FCSTD DOCUMENT  (FreeCAD 0.17R11580 (Git))
Label: connector_positions
License: All rights reserved
LicenseURL: http://en.wikipedia.org/wiki/All_rights_reserved
objects: Sketcher::SketchObject×2
note: 2 computed .brp shape members not serialized (recipe doc carries the construction recipe); baked Part::Feature solids carry a one-line shape summary decoded from their .brp

FEATURE [Sketcher::SketchObject] Sketch  label="old"
  sketch-geometry (28):
    g0: LineSegment StartX=-20 StartY=20 StartZ=0 EndX=20 EndY=20 EndZ=0
    g1: LineSegment StartX=20 StartY=20 StartZ=0 EndX=20 EndY=-20 EndZ=0
    g2: LineSegment StartX=20 StartY=-20 StartZ=0 EndX=-20 EndY=-20 EndZ=0
    g3: LineSegment StartX=-20 StartY=-20 StartZ=0 EndX=-20 EndY=20 EndZ=0
    g4: Circle CenterX=-9.81 CenterY=-18 CenterZ=0 NormalX=0 NormalY=0 NormalZ=1 Radius=0.5
    g5: Circle CenterX=-7.27 CenterY=-18 CenterZ=0 NormalX=0 NormalY=0 NormalZ=1 Radius=0.5
    g6: LineSegment [constr] StartX=-9.81 StartY=-18 StartZ=0 EndX=-7.27 EndY=-18 EndZ=0
    g7: Circle CenterX=-4.73 CenterY=-18 CenterZ=0 NormalX=0 NormalY=0 NormalZ=1 Radius=0.5
    g8: LineSegment [constr] StartX=-7.27 StartY=-18 StartZ=0 EndX=-4.73 EndY=-18 EndZ=0
    g9: Circle CenterX=-2.19 CenterY=-18 CenterZ=0 NormalX=0 NormalY=0 NormalZ=1 Radius=0.5
    g10: LineSegment [constr] StartX=-4.73 StartY=-18 StartZ=0 EndX=-2.19 EndY=-18 EndZ=0
    g11: Circle CenterX=2.19 CenterY=-18 CenterZ=0 NormalX=0 NormalY=0 NormalZ=1 Radius=0.5
    g12: Circle CenterX=4.73 CenterY=-18 CenterZ=0 NormalX=0 NormalY=0 NormalZ=1 Radius=0.5
    g13: LineSegment [constr] StartX=2.19 StartY=-18 StartZ=0 EndX=4.73 EndY=-18 EndZ=0
    g14: Circle CenterX=7.27 CenterY=-18 CenterZ=0 NormalX=0 NormalY=0 NormalZ=1 Radius=0.5
    g15: LineSegment [constr] StartX=4.73 StartY=-18 StartZ=0 EndX=7.27 EndY=-18 EndZ=0
    g16: Circle CenterX=9.81 CenterY=-18 CenterZ=0 NormalX=0 NormalY=0 NormalZ=1 Radius=0.5
    g17: LineSegment [constr] StartX=7.27 StartY=-18 StartZ=0 EndX=9.81 EndY=-18 EndZ=0
    g18: Circle CenterX=-17.27 CenterY=-18 CenterZ=0 NormalX=0 NormalY=0 NormalZ=1 Radius=0.5
    g19: Circle CenterX=-14.73 CenterY=-18 CenterZ=0 NormalX=0 NormalY=0 NormalZ=1 Radius=0.5
    g20: LineSegment [constr] StartX=-17.27 StartY=-18 StartZ=0 EndX=-14.73 EndY=-18 EndZ=0
    g21: Circle CenterX=14.73 CenterY=-18 CenterZ=0 NormalX=0 NormalY=0 NormalZ=1 Radius=0.5
    g22: Circle CenterX=17.27 CenterY=-18 CenterZ=0 NormalX=0 NormalY=0 NormalZ=1 Radius=0.5
    g23: LineSegment [constr] StartX=14.73 StartY=-18 StartZ=0 EndX=17.27 EndY=-18 EndZ=0
    g24: GeomPoint X=-16 Y=-18 Z=0
    g25: GeomPoint X=-6 Y=-18 Z=0
    g26: GeomPoint X=6 Y=-18 Z=0
    g27: GeomPoint X=16 Y=-18 Z=0
  constraints (72):
    c: Coincident(g0,g1)
    c: Coincident(g1,g2)
    c: Coincident(g2,g3)
    c: Coincident(g3,g0)
    c: Horizontal(g0)
    c: Horizontal(g2)
    c: Vertical(g1)
    c: Vertical(g3)
    c: Equal(g0,g1)
    c: Symmetric(g0,g2,g-1)
    c: DistanceX(g0,g0) = 40
    c: Radius(g4) = 0.5
    c: Equal(g4,g5) = 0.5
    c: Coincident(g4,g6)
    c: Coincident(g5,g6)
    c: Distance(g6) = 2.54
    c: Equal(g4,g7) = 0.5
    c: Coincident(g5,g8)
    c: Coincident(g7,g8)
    c: Equal(g6,g8)
    c: Parallel(g8,g6)
    c: Equal(g4,g9) = 0.5
    c: Coincident(g7,g10)
    c: Coincident(g9,g10)
    c: Equal(g6,g10)
    c: Parallel(g10,g6)
    c: Horizontal(g6)
    c: Equal(g4,g11) = 0.5
    c: Equal(g11,g12) = 0.5
    c: Coincident(g11,g13)
    c: Coincident(g12,g13)
    c: Equal(g6,g13) = 2.54
    c: Equal(g11,g14) = 0.5
    c: Coincident(g12,g15)
    c: Coincident(g14,g15)
    c: Equal(g13,g15)
    c: Parallel(g15,g13)
    c: Equal(g11,g16) = 0.5
    c: Coincident(g14,g17)
    c: Coincident(g16,g17)
    c: Equal(g13,g17)
    c: Parallel(g17,g13)
    c: Horizontal(g13)
    c: Equal(g4,g18) = 0.5
    c: Coincident(g18,g20)
    c: Coincident(g19,g20)
    c: Distance(g20) = 2.54
    c: Horizontal(g20)
    c: Coincident(g21,g23)
    c: Coincident(g22,g23)
    c: Equal(g20,g23) = 2.54
    c: Horizontal(g23)
    c: Symmetric(g23,g23,g27)
    c: Symmetric(g15,g15,g26)
    c: Symmetric(g20,g20,g24)
    c: Symmetric(g8,g8,g25)
    c: DistanceX(g24,g2) = -4
    c: DistanceY(g24,g2) = -2
    c: DistanceX(g27,g1) = 4
    c: DistanceX(g2,g18) = 2.73
    c: DistanceX(g2,g21) = 34.73
    c: DistanceX(g2,g11) = 22.19
    c: DistanceX(g2,g4) = 10.19
    c: DistanceX(g2,g25) = 14
    c: PointOnObject(g4,g20)
    c: PointOnObject(g11,g20)
    c: PointOnObject(g21,g20)
    c: DistanceX(g2,g26) = 26
    c: DistanceX(g26,g1) = 14
    c: Equal(g19,g18)
    c: Equal(g22,g21)
    c: Equal(g21,g18)
FEATURE [Sketcher::SketchObject] Sketch001  label="connector_positions"
  sketch-geometry (24):
    g0: LineSegment StartX=-20 StartY=20 StartZ=0 EndX=20 EndY=20 EndZ=0
    g1: LineSegment StartX=20 StartY=20 StartZ=0 EndX=20 EndY=-20 EndZ=0
    g2: LineSegment StartX=20 StartY=-20 StartZ=0 EndX=-20 EndY=-20 EndZ=0
    g3: LineSegment StartX=-20 StartY=-20 StartZ=0 EndX=-20 EndY=20 EndZ=0
    g4: Circle CenterX=-6.35 CenterY=-18 CenterZ=0 NormalX=0 NormalY=0 NormalZ=1 Radius=0.5
    g5: Circle CenterX=-3.81 CenterY=-18 CenterZ=0 NormalX=0 NormalY=0 NormalZ=1 Radius=0.5
    g6: LineSegment [constr] StartX=-6.35 StartY=-18 StartZ=0 EndX=-3.81 EndY=-18 EndZ=0
    g7: Circle CenterX=-1.27 CenterY=-18 CenterZ=0 NormalX=0 NormalY=0 NormalZ=1 Radius=0.5
    g8: LineSegment [constr] StartX=-3.81 StartY=-18 StartZ=0 EndX=-1.27 EndY=-18 EndZ=0
    g9: Circle CenterX=1.27 CenterY=-18 CenterZ=0 NormalX=0 NormalY=0 NormalZ=1 Radius=0.5
    g10: LineSegment [constr] StartX=-1.27 StartY=-18 StartZ=0 EndX=1.27 EndY=-18 EndZ=0
    g11: Circle CenterX=-16.27 CenterY=-18 CenterZ=0 NormalX=0 NormalY=0 NormalZ=1 Radius=0.5
    g12: Circle CenterX=-13.73 CenterY=-18 CenterZ=0 NormalX=0 NormalY=0 NormalZ=1 Radius=0.5
    g13: LineSegment [constr] StartX=-16.27 StartY=-18 StartZ=0 EndX=-13.73 EndY=-18 EndZ=0
    g14: Circle CenterX=13.73 CenterY=-18 CenterZ=0 NormalX=0 NormalY=0 NormalZ=1 Radius=0.5
    g15: Circle CenterX=16.27 CenterY=-18 CenterZ=0 NormalX=0 NormalY=0 NormalZ=1 Radius=0.5
    g16: LineSegment [constr] StartX=13.73 StartY=-18 StartZ=0 EndX=16.27 EndY=-18 EndZ=0
    g17: GeomPoint X=-15 Y=-18 Z=0
    g18: GeomPoint X=0 Y=-18 Z=0
    g19: GeomPoint X=15 Y=-18 Z=0
    g20: Circle CenterX=6.35 CenterY=-18 CenterZ=0 NormalX=0 NormalY=0 NormalZ=1 Radius=0.5
    g21: Circle CenterX=3.81 CenterY=-18 CenterZ=0 NormalX=0 NormalY=0 NormalZ=1 Radius=0.5
    g22: LineSegment [constr] StartX=3.81 StartY=-18 StartZ=0 EndX=6.35 EndY=-18 EndZ=0
    g23: LineSegment [constr] StartX=1.27 StartY=-18 StartZ=0 EndX=3.81 EndY=-18 EndZ=0
  constraints (61):
    c: Coincident(g0,g1)
    c: Coincident(g1,g2)
    c: Coincident(g2,g3)
    c: Coincident(g3,g0)
    c: Horizontal(g0)
    c: Horizontal(g2)
    c: Vertical(g1)
    c: Vertical(g3)
    c: Equal(g0,g1)
    c: Symmetric(g0,g2,g-1)
    c: DistanceX(g0,g0) = 40
    c: Radius(g4) = 0.5
    c: Equal(g4,g5) = 0.5
    c: Coincident(g4,g6)
    c: Coincident(g5,g6)
    c: Distance(g6) = 2.54
    c: Equal(g4,g7) = 0.5
    c: Coincident(g5,g8)
    c: Coincident(g7,g8)
    c: Equal(g6,g8)
    c: Parallel(g8,g6)
    c: Equal(g4,g9) = 0.5
    c: Coincident(g7,g10)
    c: Coincident(g9,g10)
    c: Equal(g6,g10)
    c: Parallel(g10,g6)
    c: Horizontal(g6)
    c: Equal(g4,g11) = 0.5
    c: Coincident(g11,g13)
    c: Coincident(g12,g13)
    c: Distance(g13) = 2.54
    c: Horizontal(g13)
    c: Coincident(g14,g16)
    c: Coincident(g15,g16)
    c: Equal(g13,g16) = 2.54
    c: Horizontal(g16)
    c: Symmetric(g16,g16,g19)
    c: Symmetric(g13,g13,g17)
    c: DistanceX(g17,g2) = -5
    c: DistanceY(g17,g2) = -2
    c: DistanceX(g19,g1) = 5
    c: DistanceX(g2,g11) = 3.73
    c: DistanceX(g2,g14) = 33.73
    c: DistanceX(g2,g4) = 13.65
    c: DistanceX(g2,g18) = 20
    c: PointOnObject(g4,g13)
    c: PointOnObject(g14,g13)
    c: Equal(g12,g11)
    c: Equal(g15,g14)
    c: Equal(g14,g11)
    c: Coincident(g21,g23)
    c: Coincident(g21,g22)
    c: Coincident(g20,g22)
    c: Coincident(g23,g9)
    c: Equal(g6,g23)
    c: Equal(g23,g22)
    c: Horizontal(g23)
    c: Horizontal(g22)
    c: Equal(g20,g21)
    c: Equal(g21,g9)
    c: Symmetric(g10,g10,g18)
